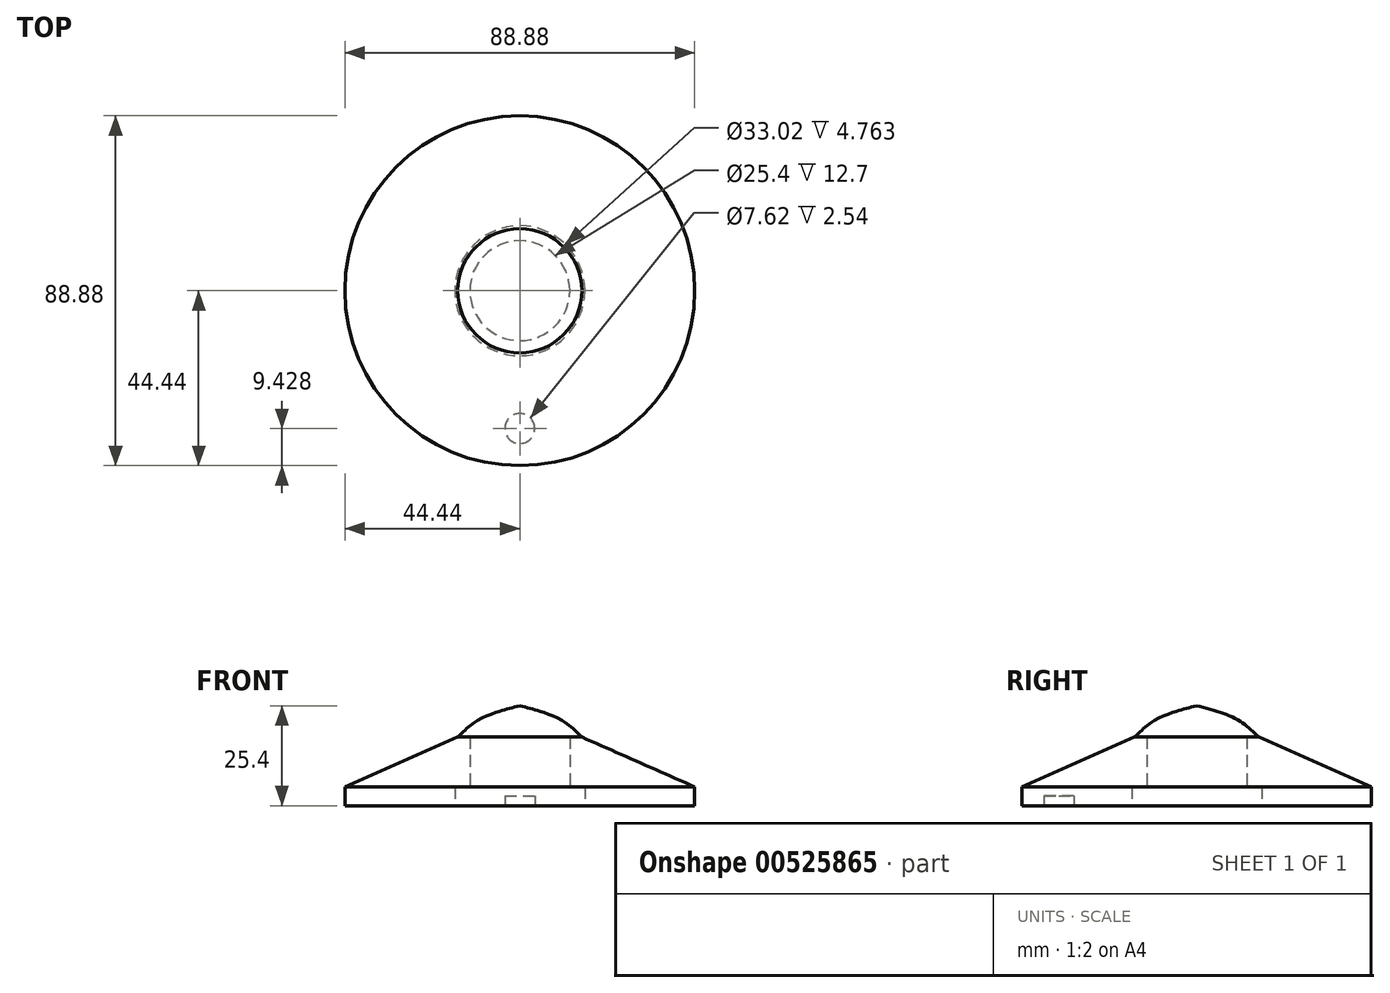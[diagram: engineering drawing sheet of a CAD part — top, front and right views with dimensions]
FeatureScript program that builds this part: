
annotation { "Feature Type Name" : "Feature", "Feature Type Description" : "" }
export const myFeature = defineFeature(function(context is Context, id is Id, definition is map)
    precondition{}
    {
        {
            var Q0;
            Q0=qCreatedBy(makeId("Right.planeOp"),FACE);
            var sketch = newSketch(context, id + "F0", { "sketchPlane" : qUnion([Q0])});
            skLineSegment(sketch, "E0", {"start": v(0, 0) * mm, "end": v(44.44, 0) * mm});
            skLineSegment(sketch, "E1", {"start": v(44.44, 0) * mm, "end": v(44.44, 4.77) * mm});
            skFitSpline(sketch, "E2", {"points": [v(0, 25.4) * mm, v(10.23, 21.94) * mm, v(15.76, 17.42) * mm], "startDerivative": vector(20.27, -5.22) * mm, "endDerivative": vector(10.94, -10.95) * mm});
            skLineSegment(sketch, "E3", {"start": v(15.76, 17.42) * mm, "end": v(44.44, 4.77) * mm});
            skLineSegment(sketch, "E4", {"start": v(0, 25.4) * mm, "end": v(0, 0) * mm});
            skSolve(sketch);
        }
        {
            var Q0;
            Q0=makeQuery(id+"F0.imprint","IMPRINT",FACE,{"disambiguationData":[TD([[makeQuery(id+"F0.imprint","IMPRINT",EDGE,{"derivedFrom":sQuery(id+"F0.wireOp",EDGE,"E0")}),1.0]])]});
            var Q1;
            Q1=sQuery(id+"F0.wireOp",EDGE,"E4");
            revolve(context, id + "F1", {"entities" : qUnion([Q0]), "axis" : qUnion([Q1]), "revolveType" : RevolveType.FULL});
        }
        {
            var Q0;
            Q0=makeQuery(id+"F1.opRevolve","SWEPT_FACE",FACE,{"disambiguationData":[OSD([sQuery(id+"F0.wireOp",EDGE,"E0")])]});
            var sketch = newSketch(context, id + "F2", { "sketchPlane" : qUnion([Q0])});
            skCircle(sketch, "E5", {"center": v(0, 0) * mm, "radius": 16.51 * mm});
            skSolve(sketch);
        }
        {
            var Q0;
            Q0 = qSketchRegion(id + "F2", true);
            extrude(context, id + "F3", {"entities" : qUnion([Q0]), "operationType" : NewBodyOperationType.REMOVE, "oppositeDirection" : true, "depth" : 4.76 * mm, "offsetDistance" : 25.4 * mm});
        }
        {
            var Q0;
            Q0=makeQuery(id+"F3.boolean.opBoolean","COPY",FACE,{"derivedFrom":makeQuery(id+"F3.opExtrude","CAP_FACE",FACE,{"disambiguationData":[OSD([sQuery(id+"F2.wireOp",EDGE,"E5")])],"isStart":false})});
            var sketch = newSketch(context, id + "F4", { "sketchPlane" : qUnion([Q0])});
            skCircle(sketch, "E6", {"center": v(0, 0) * mm, "radius": 12.7 * mm});
            skSolve(sketch);
        }
        {
            var Q0;
            Q0 = qSketchRegion(id + "F4", true);
            extrude(context, id + "F5", {"entities" : qUnion([Q0]), "operationType" : NewBodyOperationType.REMOVE, "oppositeDirection" : true, "depth" : 12.7 * mm, "offsetDistance" : 25.4 * mm});
        }
        {
            var Q0;
            Q0=makeQuery(id+"F1.opRevolve","SWEPT_FACE",FACE,{"disambiguationData":[OSD([sQuery(id+"F0.wireOp",EDGE,"E0")])]});
            var sketch = newSketch(context, id + "F6", { "sketchPlane" : qUnion([Q0])});
            skCircle(sketch, "E7", {"center": v(0, 35.01) * mm, "radius": 3.81 * mm});
            skSolve(sketch);
        }
        {
            var Q0;
            Q0=makeQuery(id+"F6.imprint","IMPRINT",FACE,{"disambiguationData":[TD([[makeQuery(id+"F6.imprint","IMPRINT",EDGE,{"derivedFrom":sQuery(id+"F6.wireOp",EDGE,"E7")}),1.0]])]});
            extrude(context, id + "F7", {"entities" : qUnion([Q0]), "operationType" : NewBodyOperationType.REMOVE, "oppositeDirection" : true, "depth" : 2.54 * mm, "offsetDistance" : 25.4 * mm});
        }
    });
